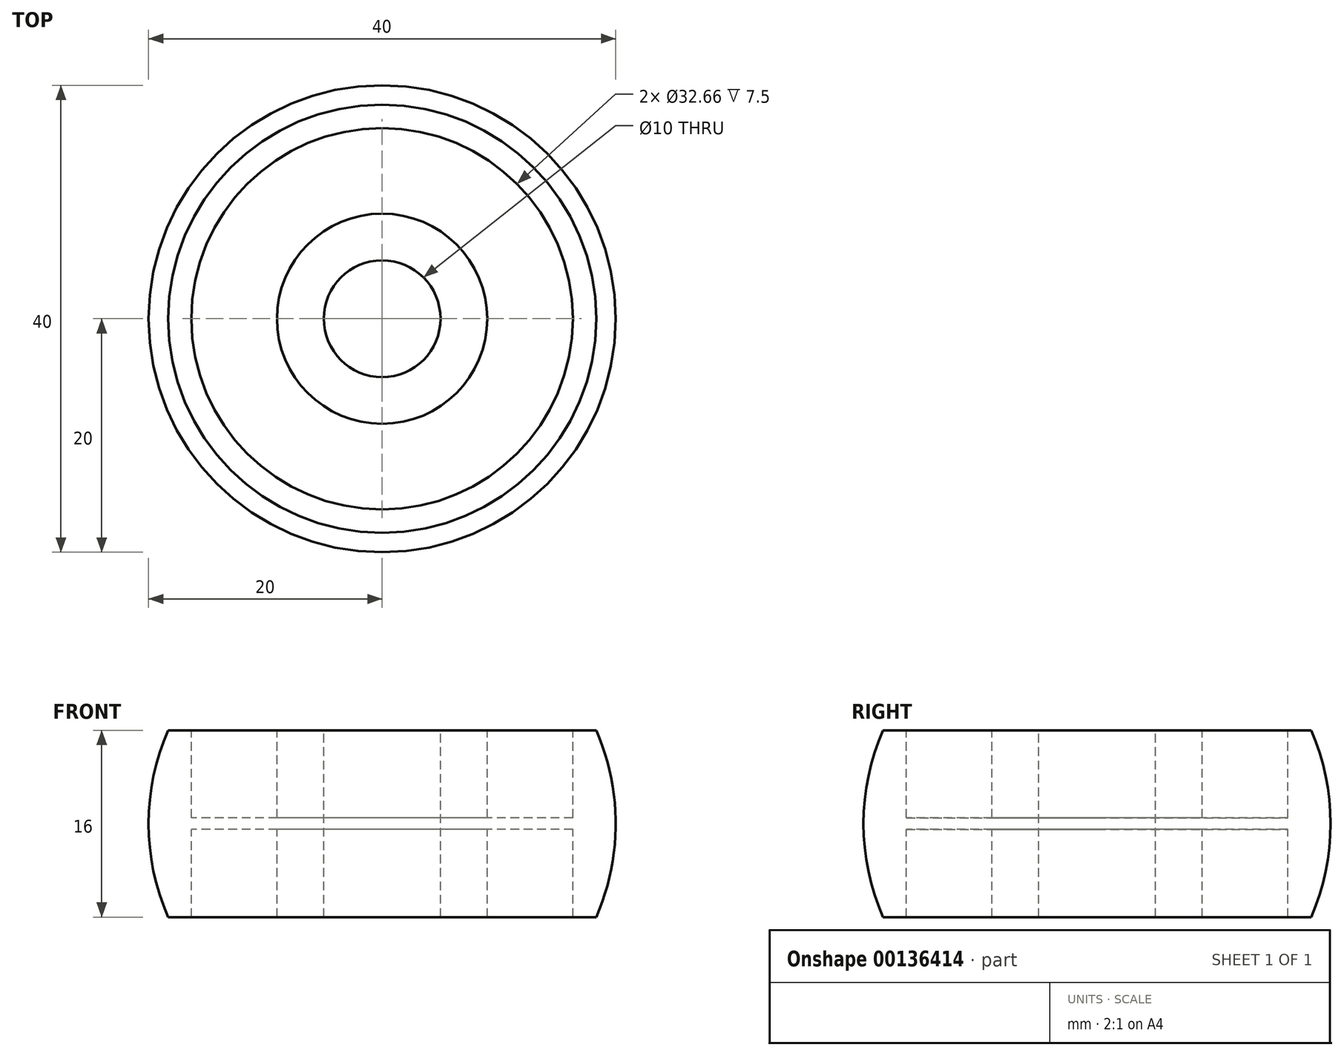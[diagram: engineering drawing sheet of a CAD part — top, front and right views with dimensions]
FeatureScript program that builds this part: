
annotation { "Feature Type Name" : "Feature", "Feature Type Description" : "" }
export const myFeature = defineFeature(function(context is Context, id is Id, definition is map)
    precondition{}
    {
        {
            var Q0;
            Q0=qCreatedBy(makeId("Front.planeOp"),FACE);
            var sketch = newSketch(context, id + "F0", { "sketchPlane" : qUnion([Q0])});
            skCircle(sketch, "E0", {"center": v(0, 0) * mm, "radius": 20 * mm});
            skLineSegment(sketch, "E1", {"start": v(0, 8) * mm, "end": v(0, -8) * mm, "construction": true});
            skLineSegment(sketch, "E2", {"start": v(0, 8) * mm, "end": v(9, 8) * mm});
            skLineSegment(sketch, "E3", {"start": v(5, 8) * mm, "end": v(5, -8) * mm});
            skLineSegment(sketch, "E4.MirrorCS", {"start": v(0, -8) * mm, "end": v(9, -8) * mm});
            skLineSegment(sketch, "E5", {"start": v(9, 8) * mm, "end": v(9, 0.5) * mm});
            skLineSegment(sketch, "E6", {"start": v(9, 0.5) * mm, "end": v(16.33, 0.5) * mm});
            skLineSegment(sketch, "E7", {"start": v(16.33, 0.5) * mm, "end": v(16.33, 8) * mm});
            skLineSegment(sketch, "E8", {"start": v(16.33, 8) * mm, "end": v(18.33, 8) * mm});
            skLineSegment(sketch, "E9.MirrorCS", {"start": v(9, -0.5) * mm, "end": v(16.33, -0.5) * mm});
            skLineSegment(sketch, "E10.MirrorCS", {"start": v(9, -8) * mm, "end": v(9, -0.5) * mm});
            skLineSegment(sketch, "E11.MirrorCS", {"start": v(16.33, -0.5) * mm, "end": v(16.33, -8) * mm});
            skLineSegment(sketch, "E12.MirrorCS", {"start": v(16.33, -8) * mm, "end": v(18.33, -8) * mm});
            skSolve(sketch);
        }
        {
            var Q0;
            {var subQ5=sQuery(id+"F0.wireOp",EDGE,"E3");Q0=makeQuery(id+"F0.imprint","IMPRINT",FACE,{"disambiguationData":[TD([[makeQuery(id+"F0.imprint","IMPRINT",EDGE,{"derivedFrom":subQ5}),1.0]])]});}
            var Q1;
            Q1=sQuery(id+"F0.wireOp",EDGE,"E1");
            revolve(context, id + "F1", {"entities" : qUnion([Q0]), "axis" : qUnion([Q1]), "revolveType" : RevolveType.FULL});
        }
    });
